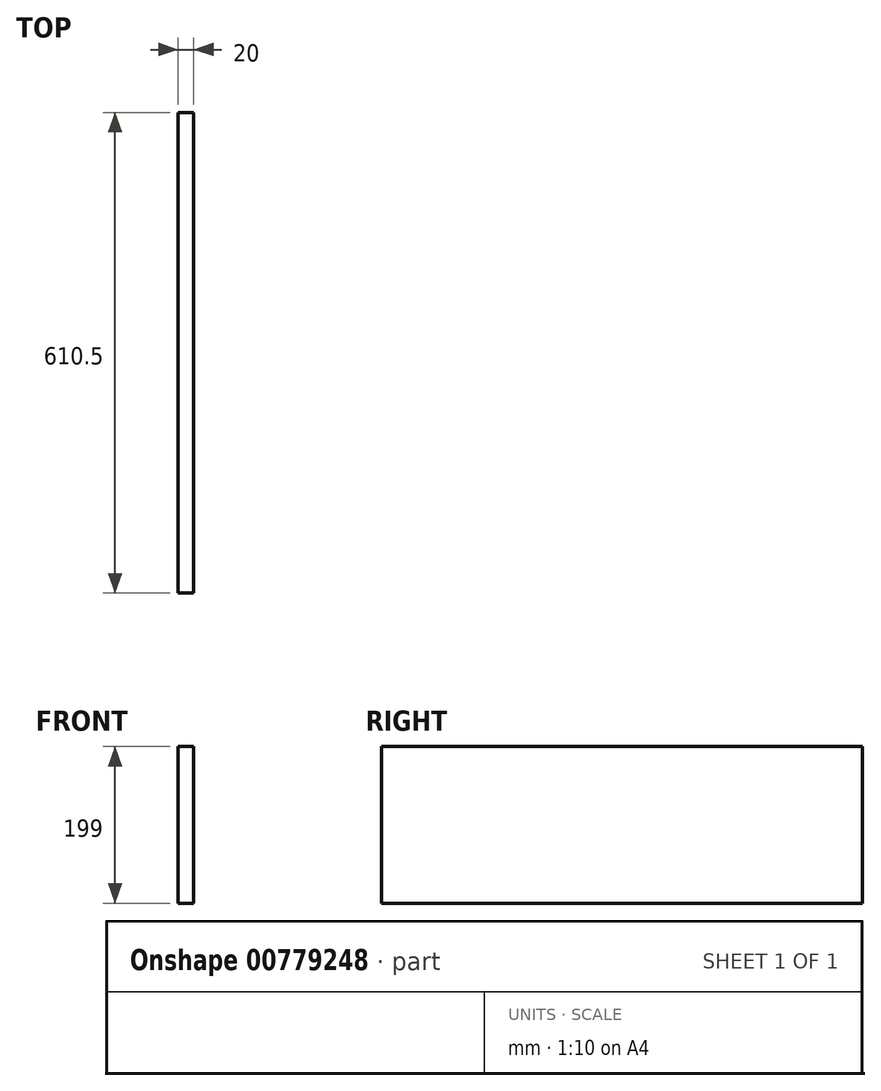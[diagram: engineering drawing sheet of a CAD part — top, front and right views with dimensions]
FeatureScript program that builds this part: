
annotation { "Feature Type Name" : "Feature", "Feature Type Description" : "" }
export const myFeature = defineFeature(function(context is Context, id is Id, definition is map)
    precondition{}
    {
        {
            var Q0;
            Q0=qCreatedBy(makeId("Front.planeOp"),FACE);
            var sketch = newSketch(context, id + "F0", { "sketchPlane" : qUnion([Q0])});
            skLineSegment(sketch, "E0.bottom", {"start": v(0, 0) * mm, "end": v(20, 0) * mm});
            skLineSegment(sketch, "E0.top", {"start": v(0, 199) * mm, "end": v(20, 199) * mm});
            skLineSegment(sketch, "E0.left", {"start": v(0, 0) * mm, "end": v(0, 199) * mm});
            skLineSegment(sketch, "E0.right", {"start": v(20, 0) * mm, "end": v(20, 199) * mm});
            skSolve(sketch);
        }
        {
            var Q0;
            Q0=qSketchRegion(id+"F0",true);
            extrude(context, id + "F1", {"entities" : qUnion([Q0]), "depth" : 610.5 * mm});
        }
    });
